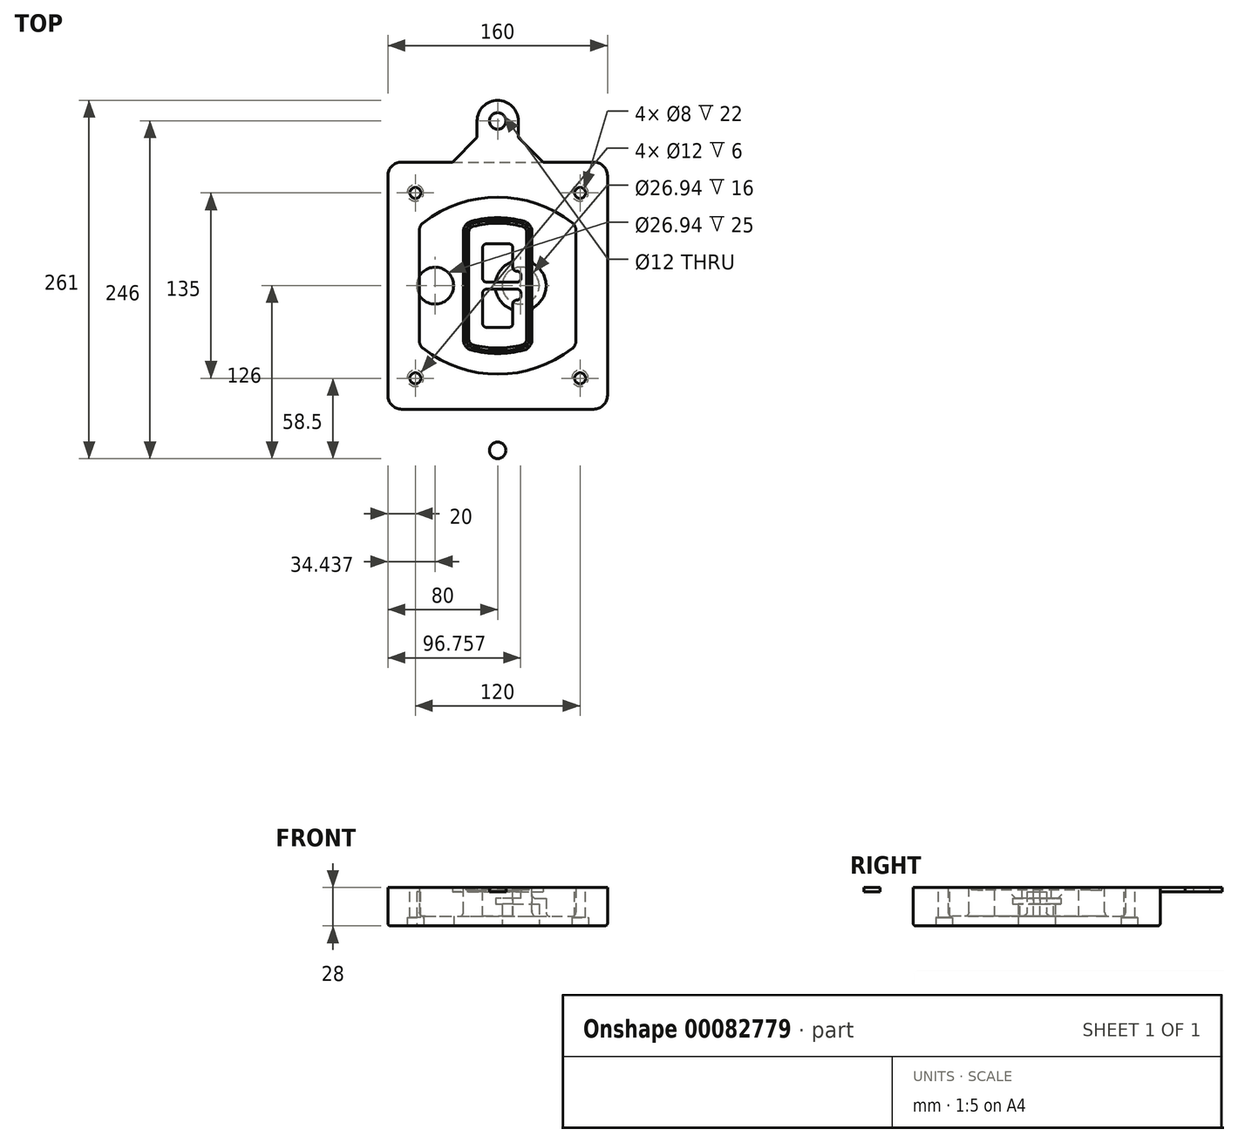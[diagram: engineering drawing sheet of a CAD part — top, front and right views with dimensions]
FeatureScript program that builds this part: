
annotation { "Feature Type Name" : "Feature", "Feature Type Description" : "" }
export const myFeature = defineFeature(function(context is Context, id is Id, definition is map)
    precondition{}
    {
        {
            var Q0;
            Q0=qCreatedBy(makeId("Top.planeOp"),FACE);
            var sketch = newSketch(context, id + "F0", { "sketchPlane" : qUnion([Q0])});
            skPoint(sketch, "E0.rect.middle", {"position": v(0, 0) * mm});
            skLineSegment(sketch, "E1.bottom", {"start": v(-70, -90) * mm, "end": v(70, -90) * mm});
            skLineSegment(sketch, "E1.top", {"start": v(-70, 90) * mm, "end": v(70, 90) * mm});
            skLineSegment(sketch, "E1.left", {"start": v(-80, -80) * mm, "end": v(-80, 80) * mm});
            skLineSegment(sketch, "E1.right", {"start": v(80, -80) * mm, "end": v(80, 80) * mm});
            skLineSegment(sketch, "E2", {"start": v(-80, 90) * mm, "end": v(80, -90) * mm, "construction": true});
            skLineSegment(sketch, "E3", {"start": v(80, 90) * mm, "end": v(-80, -90) * mm, "construction": true});
            skCircle(sketch, "E4", {"center": v(-60, 67.5) * mm, "radius": 4 * mm});
            skCircle(sketch, "E5", {"center": v(60, 67.5) * mm, "radius": 4 * mm});
            skCircle(sketch, "E6", {"center": v(60, -67.5) * mm, "radius": 4 * mm});
            skCircle(sketch, "E7", {"center": v(-60, -67.5) * mm, "radius": 4 * mm});
            skLineSegment(sketch, "E8", {"start": v(-60, 67.5) * mm, "end": v(60, 67.5) * mm, "construction": true});
            skLineSegment(sketch, "E9", {"start": v(60, 67.5) * mm, "end": v(60, -67.5) * mm, "construction": true});
            skLineSegment(sketch, "E10", {"start": v(60, -67.5) * mm, "end": v(-60, -67.5) * mm, "construction": true});
            skLineSegment(sketch, "E11", {"start": v(-60, -67.5) * mm, "end": v(-60, 67.5) * mm, "construction": true});
            skLineSegment(sketch, "E12", {"start": v(-60, 40.3) * mm, "end": v(-60, -40.3) * mm});
            skLineSegment(sketch, "E13", {"start": v(60, 40.3) * mm, "end": v(60, -40.3) * mm});
            skArc(sketch, "E14", {"start": v(56.15, 48.18) * mm, "mid": v(0, 67.5) * mm, "end": v(-56.15, 48.18) * mm});
            skArc(sketch, "E15", {"start": v(-56.15, -48.18) * mm, "mid": v(0, -67.5) * mm, "end": v(56.15, -48.18) * mm});
            skLineSegment(sketch, "E16", {"start": v(-60, 0) * mm, "end": v(60, 0) * mm, "construction": true});
            skPoint(sketch, "E17.visualSharp", {"position": v(-60, -45) * mm});
            skArc(sketch, "E17.filletArc", {"start": v(-60, -40.3) * mm, "mid": v(-58.99, -44.68) * mm, "end": v(-56.15, -48.18) * mm});
            skPoint(sketch, "E18.visualSharp", {"position": v(-60, 45) * mm});
            skArc(sketch, "E18.filletArc", {"start": v(-56.15, 48.18) * mm, "mid": v(-58.99, 44.68) * mm, "end": v(-60, 40.3) * mm});
            skPoint(sketch, "E19.visualSharp", {"position": v(60, 45) * mm});
            skArc(sketch, "E19.filletArc", {"start": v(60, 40.3) * mm, "mid": v(58.99, 44.68) * mm, "end": v(56.15, 48.18) * mm});
            skPoint(sketch, "E20.visualSharp", {"position": v(60, -45) * mm});
            skArc(sketch, "E20.filletArc", {"start": v(56.15, -48.18) * mm, "mid": v(58.99, -44.68) * mm, "end": v(60, -40.3) * mm});
            skPoint(sketch, "E21.visualSharp", {"position": v(-80, 90) * mm});
            skArc(sketch, "E21.filletArc", {"start": v(-70, 90) * mm, "mid": v(-77.07, 87.07) * mm, "end": v(-80, 80) * mm});
            skPoint(sketch, "E22.visualSharp", {"position": v(80, 90) * mm});
            skArc(sketch, "E22.filletArc", {"start": v(80, 80) * mm, "mid": v(77.07, 87.07) * mm, "end": v(70, 90) * mm});
            skPoint(sketch, "E23.visualSharp", {"position": v(80, -90) * mm});
            skArc(sketch, "E23.filletArc", {"start": v(70, -90) * mm, "mid": v(77.07, -87.07) * mm, "end": v(80, -80) * mm});
            skPoint(sketch, "E24.visualSharp", {"position": v(-80, -90) * mm});
            skArc(sketch, "E24.filletArc", {"start": v(-80, -80) * mm, "mid": v(-77.07, -87.07) * mm, "end": v(-70, -90) * mm});
            skArc(sketch, "E25.0", {"start": v(57, 40.3) * mm, "mid": v(56.3, 43.36) * mm, "end": v(54.3, 45.81) * mm});
            skLineSegment(sketch, "E25.1", {"start": v(57, 40.3) * mm, "end": v(57, -40.3) * mm});
            skArc(sketch, "E25.2", {"start": v(54.3, -45.81) * mm, "mid": v(56.3, -43.36) * mm, "end": v(57, -40.3) * mm});
            skArc(sketch, "E25.3", {"start": v(-54.3, -45.81) * mm, "mid": v(0, -64.5) * mm, "end": v(54.3, -45.81) * mm});
            skArc(sketch, "E25.4", {"start": v(-57, -40.3) * mm, "mid": v(-56.3, -43.36) * mm, "end": v(-54.3, -45.81) * mm});
            skArc(sketch, "E25.5", {"start": v(54.3, 45.81) * mm, "mid": v(0, 64.5) * mm, "end": v(-54.3, 45.81) * mm});
            skLineSegment(sketch, "E25.6", {"start": v(-57, 40.3) * mm, "end": v(-57, -40.3) * mm});
            skArc(sketch, "E25.7", {"start": v(-54.3, 45.81) * mm, "mid": v(-56.3, 43.36) * mm, "end": v(-57, 40.3) * mm});
            skArc(sketch, "E26.0", {"start": v(-58.62, 51.33) * mm, "mid": v(-62.58, 46.43) * mm, "end": v(-64, 40.3) * mm});
            skArc(sketch, "E26.1", {"start": v(58.62, 51.33) * mm, "mid": v(0, 71.5) * mm, "end": v(-58.62, 51.33) * mm});
            skArc(sketch, "E26.2", {"start": v(64, 40.3) * mm, "mid": v(62.58, 46.43) * mm, "end": v(58.62, 51.33) * mm});
            skLineSegment(sketch, "E26.3", {"start": v(64, 40.3) * mm, "end": v(64, -40.3) * mm});
            skArc(sketch, "E26.4", {"start": v(58.62, -51.33) * mm, "mid": v(62.58, -46.43) * mm, "end": v(64, -40.3) * mm});
            skLineSegment(sketch, "E26.5", {"start": v(-64, 40.3) * mm, "end": v(-64, -40.3) * mm});
            skArc(sketch, "E26.6", {"start": v(-58.62, -51.33) * mm, "mid": v(0, -71.5) * mm, "end": v(58.62, -51.33) * mm});
            skArc(sketch, "E26.7", {"start": v(-64, -40.3) * mm, "mid": v(-62.58, -46.43) * mm, "end": v(-58.62, -51.33) * mm});
            skSolve(sketch);
        }
        {
            var Q0;
            Q0=makeQuery(id+"F0.imprint","IMPRINT",FACE,{"disambiguationData":[TD([[makeQuery(id+"F0.imprint","IMPRINT",EDGE,{"derivedFrom":sQuery(id+"F0.wireOp",EDGE,"E1.bottom")}),1.0]])]});
            var Q1;
            Q1=makeQuery(id+"F0.imprint","IMPRINT",FACE,{"disambiguationData":[TD([[makeQuery(id+"F0.imprint","IMPRINT",EDGE,{"derivedFrom":sQuery(id+"F0.wireOp",EDGE,"E12")}),1.0]])]});
            var Q2;
            Q2=makeQuery(id+"F0.imprint","IMPRINT",FACE,{"disambiguationData":[TD([[makeQuery(id+"F0.imprint","IMPRINT",EDGE,{"derivedFrom":sQuery(id+"F0.wireOp",EDGE,"E25.0")}),1.0]])]});
            var Q3;
            Q3=makeQuery(id+"F0.imprint","IMPRINT",FACE,{"disambiguationData":[TD([[makeQuery(id+"F0.imprint","IMPRINT",EDGE,{"derivedFrom":sQuery(id+"F0.wireOp",EDGE,"E12")}),-1.0]])]});
            extrude(context, id + "F1", {"entities" : qUnion([Q0, Q1, Q2, Q3]), "oppositeDirection" : true, "depth" : 25 * mm});
        }
        {
            var Q0;
            Q0=makeQuery(id+"F0.imprint","IMPRINT",FACE,{"disambiguationData":[TD([[makeQuery(id+"F0.imprint","IMPRINT",EDGE,{"derivedFrom":sQuery(id+"F0.wireOp",EDGE,"E12")}),1.0]])]});
            extrude(context, id + "F2", {"entities" : qUnion([Q0]), "operationType" : NewBodyOperationType.ADD, "depth" : 3 * mm});
        }
        {
            var Q0;
            Q0=makeQuery(id+"F0.imprint","IMPRINT",FACE,{"disambiguationData":[TD([[makeQuery(id+"F0.imprint","IMPRINT",EDGE,{"derivedFrom":sQuery(id+"F0.wireOp",EDGE,"E25.0")}),1.0]])]});
            extrude(context, id + "F3", {"entities" : qUnion([Q0]), "operationType" : NewBodyOperationType.REMOVE, "oppositeDirection" : true, "depth" : 18 * mm});
        }
        {
            var Q0;
            Q0=makeQuery(id+"F2.opExtrude","CAP_FACE",FACE,{"disambiguationData":[OSD([sQuery(id+"F0.wireOp",EDGE,"E12"),sQuery(id+"F0.wireOp",EDGE,"E13"),sQuery(id+"F0.wireOp",EDGE,"E14"),sQuery(id+"F0.wireOp",EDGE,"E15"),sQuery(id+"F0.wireOp",EDGE,"E17.filletArc"),sQuery(id+"F0.wireOp",EDGE,"E18.filletArc"),sQuery(id+"F0.wireOp",EDGE,"E19.filletArc"),sQuery(id+"F0.wireOp",EDGE,"E20.filletArc"),sQuery(id+"F0.wireOp",EDGE,"E25.0"),sQuery(id+"F0.wireOp",EDGE,"E25.1"),sQuery(id+"F0.wireOp",EDGE,"E25.2"),sQuery(id+"F0.wireOp",EDGE,"E25.3"),sQuery(id+"F0.wireOp",EDGE,"E25.4"),sQuery(id+"F0.wireOp",EDGE,"E25.5"),sQuery(id+"F0.wireOp",EDGE,"E25.6"),sQuery(id+"F0.wireOp",EDGE,"E25.7")])],"isStart":false});
            var sketch = newSketch(context, id + "F4", { "sketchPlane" : qUnion([Q0])});
            skArc(sketch, "E27.0", {"start": v(-19.08, -46.97) * mm, "mid": v(0, -49.5) * mm, "end": v(19.08, -46.97) * mm});
            skArc(sketch, "E28.0", {"start": v(19.08, 46.97) * mm, "mid": v(0, 49.5) * mm, "end": v(-19.08, 46.97) * mm});
            skLineSegment(sketch, "E29", {"start": v(-25, 39.25) * mm, "end": v(-25, -39.25) * mm});
            skLineSegment(sketch, "E30", {"start": v(25, 39.25) * mm, "end": v(25, -39.25) * mm});
            skLineSegment(sketch, "E31", {"start": v(-25, 45.1) * mm, "end": v(25, 45.1) * mm, "construction": true});
            skLineSegment(sketch, "E32", {"start": v(-25, -45.1) * mm, "end": v(25, -45.1) * mm, "construction": true});
            skPoint(sketch, "E33.visualSharp", {"position": v(-25, 45.1) * mm});
            skArc(sketch, "E33.filletArc", {"start": v(-19.08, 46.97) * mm, "mid": v(-23.35, 44.11) * mm, "end": v(-25, 39.25) * mm});
            skPoint(sketch, "E34.visualSharp", {"position": v(25, 45.1) * mm});
            skArc(sketch, "E34.filletArc", {"start": v(25, 39.25) * mm, "mid": v(23.35, 44.11) * mm, "end": v(19.08, 46.97) * mm});
            skPoint(sketch, "E35.visualSharp", {"position": v(25, -45.1) * mm});
            skArc(sketch, "E35.filletArc", {"start": v(19.08, -46.97) * mm, "mid": v(23.35, -44.11) * mm, "end": v(25, -39.25) * mm});
            skPoint(sketch, "E36.visualSharp", {"position": v(-25, -45.1) * mm});
            skArc(sketch, "E36.filletArc", {"start": v(-25, -39.25) * mm, "mid": v(-23.35, -44.11) * mm, "end": v(-19.08, -46.97) * mm});
            skArc(sketch, "E37.0", {"start": v(54.3, 45.81) * mm, "mid": v(0, 64.5) * mm, "end": v(-54.3, 45.81) * mm});
            skArc(sketch, "E37.1", {"start": v(-54.3, 45.81) * mm, "mid": v(-56.3, 43.36) * mm, "end": v(-57, 40.3) * mm});
            skLineSegment(sketch, "E37.2", {"start": v(-57, 40.3) * mm, "end": v(-57, -40.3) * mm});
            skArc(sketch, "E37.3", {"start": v(-57, -40.3) * mm, "mid": v(-56.3, -43.36) * mm, "end": v(-54.3, -45.81) * mm});
            skArc(sketch, "E37.4", {"start": v(-54.3, -45.81) * mm, "mid": v(0, -64.5) * mm, "end": v(54.3, -45.81) * mm});
            skArc(sketch, "E37.5", {"start": v(54.3, -45.81) * mm, "mid": v(56.3, -43.36) * mm, "end": v(57, -40.3) * mm});
            skLineSegment(sketch, "E37.6", {"start": v(57, 40.3) * mm, "end": v(57, -40.3) * mm});
            skArc(sketch, "E37.7", {"start": v(57, 40.3) * mm, "mid": v(56.3, 43.36) * mm, "end": v(54.3, 45.81) * mm});
            skLineSegment(sketch, "E38.0", {"start": v(23, 39.25) * mm, "end": v(23, -39.25) * mm});
            skArc(sketch, "E38.1", {"start": v(18.56, -45.04) * mm, "mid": v(21.76, -42.9) * mm, "end": v(23, -39.25) * mm});
            skArc(sketch, "E38.2", {"start": v(-18.56, -45.04) * mm, "mid": v(0, -47.5) * mm, "end": v(18.56, -45.04) * mm});
            skArc(sketch, "E38.3", {"start": v(-23, -39.25) * mm, "mid": v(-21.76, -42.9) * mm, "end": v(-18.56, -45.04) * mm});
            skLineSegment(sketch, "E38.4", {"start": v(-23, 39.25) * mm, "end": v(-23, -39.25) * mm});
            skArc(sketch, "E38.5", {"start": v(23, 39.25) * mm, "mid": v(21.76, 42.9) * mm, "end": v(18.56, 45.04) * mm});
            skArc(sketch, "E38.6", {"start": v(-18.56, 45.04) * mm, "mid": v(-21.76, 42.9) * mm, "end": v(-23, 39.25) * mm});
            skArc(sketch, "E38.7", {"start": v(18.56, 45.04) * mm, "mid": v(0, 47.5) * mm, "end": v(-18.56, 45.04) * mm});
            skArc(sketch, "E39.0", {"start": v(21, 39.25) * mm, "mid": v(20.18, 41.68) * mm, "end": v(18.04, 43.1) * mm});
            skLineSegment(sketch, "E39.1", {"start": v(21, 39.25) * mm, "end": v(21, -39.25) * mm});
            skArc(sketch, "E39.2", {"start": v(18.04, -43.1) * mm, "mid": v(20.18, -41.68) * mm, "end": v(21, -39.25) * mm});
            skArc(sketch, "E39.3", {"start": v(-18.04, -43.1) * mm, "mid": v(0, -45.5) * mm, "end": v(18.04, -43.1) * mm});
            skArc(sketch, "E39.4", {"start": v(-21, -39.25) * mm, "mid": v(-20.18, -41.68) * mm, "end": v(-18.04, -43.1) * mm});
            skArc(sketch, "E39.5", {"start": v(18.04, 43.1) * mm, "mid": v(0, 45.5) * mm, "end": v(-18.04, 43.1) * mm});
            skLineSegment(sketch, "E39.6", {"start": v(-21, 39.25) * mm, "end": v(-21, -39.25) * mm});
            skArc(sketch, "E39.7", {"start": v(-18.04, 43.1) * mm, "mid": v(-20.18, 41.68) * mm, "end": v(-21, 39.25) * mm});
            skLineSegment(sketch, "E40", {"start": v(-25, 0) * mm, "end": v(25, 0) * mm, "construction": true});
            skLineSegment(sketch, "E41", {"start": v(-11, 5.5) * mm, "end": v(-11, 27.5) * mm});
            skLineSegment(sketch, "E42", {"start": v(-8, 30.5) * mm, "end": v(8, 30.5) * mm});
            skLineSegment(sketch, "E43", {"start": v(11, 27.5) * mm, "end": v(11, 13.5) * mm});
            skLineSegment(sketch, "E44", {"start": v(14, 10.5) * mm, "end": v(14, 10.5) * mm});
            skLineSegment(sketch, "E45", {"start": v(17, 7.5) * mm, "end": v(17, 5.5) * mm});
            skLineSegment(sketch, "E46", {"start": v(14, 2.5) * mm, "end": v(-8, 2.5) * mm});
            skPoint(sketch, "E47.visualSharp", {"position": v(-11, 30.5) * mm});
            skArc(sketch, "E47.filletArc", {"start": v(-8, 30.5) * mm, "mid": v(-10.12, 29.62) * mm, "end": v(-11, 27.5) * mm});
            skPoint(sketch, "E48.visualSharp", {"position": v(11, 30.5) * mm});
            skArc(sketch, "E48.filletArc", {"start": v(11, 27.5) * mm, "mid": v(10.12, 29.62) * mm, "end": v(8, 30.5) * mm});
            skPoint(sketch, "E49.visualSharp", {"position": v(11, 10.5) * mm});
            skArc(sketch, "E49.filletArc", {"start": v(11, 13.5) * mm, "mid": v(11.88, 11.38) * mm, "end": v(14, 10.5) * mm});
            skPoint(sketch, "E50.visualSharp", {"position": v(17, 10.5) * mm});
            skArc(sketch, "E50.filletArc", {"start": v(17, 7.5) * mm, "mid": v(16.12, 9.62) * mm, "end": v(14, 10.5) * mm});
            skPoint(sketch, "E51.visualSharp", {"position": v(17, 2.5) * mm});
            skArc(sketch, "E51.filletArc", {"start": v(14, 2.5) * mm, "mid": v(16.12, 3.38) * mm, "end": v(17, 5.5) * mm});
            skPoint(sketch, "E52.visualSharp", {"position": v(-11, 2.5) * mm});
            skArc(sketch, "E52.filletArc", {"start": v(-11, 5.5) * mm, "mid": v(-10.12, 3.38) * mm, "end": v(-8, 2.5) * mm});
            skLineSegment(sketch, "E53.0.MirrorCS", {"start": v(14, -2.5) * mm, "end": v(-8, -2.5) * mm});
            skArc(sketch, "E54.0.MirrorCS", {"start": v(-11, -5.5) * mm, "mid": v(-10.12, -3.38) * mm, "end": v(-8, -2.5) * mm});
            skLineSegment(sketch, "E55.0.MirrorCS", {"start": v(-11, -5.5) * mm, "end": v(-11, -27.5) * mm});
            skArc(sketch, "E56.0.MirrorCS", {"start": v(-8, -30.5) * mm, "mid": v(-10.12, -29.62) * mm, "end": v(-11, -27.5) * mm});
            skLineSegment(sketch, "E57.0.MirrorCS", {"start": v(-8, -30.5) * mm, "end": v(8, -30.5) * mm});
            skArc(sketch, "E58.0.MirrorCS", {"start": v(11, -27.5) * mm, "mid": v(10.12, -29.62) * mm, "end": v(8, -30.5) * mm});
            skLineSegment(sketch, "E59.0.MirrorCS", {"start": v(11, -27.5) * mm, "end": v(11, -13.5) * mm});
            skArc(sketch, "E60.0.MirrorCS", {"start": v(11, -13.5) * mm, "mid": v(11.88, -11.38) * mm, "end": v(14, -10.5) * mm});
            skArc(sketch, "E61.0.MirrorCS", {"start": v(17, -7.5) * mm, "mid": v(16.12, -9.62) * mm, "end": v(14, -10.5) * mm});
            skLineSegment(sketch, "E62.0.MirrorCS", {"start": v(17, -7.5) * mm, "end": v(17, -5.5) * mm});
            skArc(sketch, "E63.0.MirrorCS", {"start": v(14, -2.5) * mm, "mid": v(16.12, -3.38) * mm, "end": v(17, -5.5) * mm});
            skSolve(sketch);
        }
        {
            var Q0;
            Q0=makeQuery(id+"F4.imprint","IMPRINT",FACE,{"disambiguationData":[TD([[makeQuery(id+"F4.imprint","IMPRINT",EDGE,{"derivedFrom":sQuery(id+"F4.wireOp",EDGE,"E27.0")}),1.0]])]});
            var Q1;
            Q1=makeQuery(id+"F4.imprint","IMPRINT",FACE,{"disambiguationData":[TD([[makeQuery(id+"F4.imprint","IMPRINT",EDGE,{"derivedFrom":sQuery(id+"F4.wireOp",EDGE,"E38.0")}),-1.0]])]});
            var Q2;
            Q2=makeQuery(id+"F4.imprint","IMPRINT",FACE,{"disambiguationData":[TD([[makeQuery(id+"F4.imprint","IMPRINT",EDGE,{"derivedFrom":sQuery(id+"F4.wireOp",EDGE,"E39.0")}),1.0]])]});
            extrude(context, id + "F5", {"entities" : qUnion([Q0, Q1, Q2]), "operationType" : NewBodyOperationType.ADD, "endBound" : BoundingType.UP_TO_NEXT, "oppositeDirection" : true, "depth" : 25 * mm});
        }
        {
            var Q0;
            Q0=makeQuery(id+"F4.imprint","IMPRINT",FACE,{"disambiguationData":[TD([[makeQuery(id+"F4.imprint","IMPRINT",EDGE,{"derivedFrom":sQuery(id+"F4.wireOp",EDGE,"E38.0")}),-1.0]])]});
            extrude(context, id + "F6", {"entities" : qUnion([Q0]), "operationType" : NewBodyOperationType.REMOVE, "oppositeDirection" : true, "depth" : 2 * mm});
        }
        {
            var Q0;
            Q0=makeQuery(id+"F1.opExtrude","CAP_FACE",FACE,{"disambiguationData":[OSD([sQuery(id+"F0.wireOp",EDGE,"E1.bottom"),sQuery(id+"F0.wireOp",EDGE,"E1.top"),sQuery(id+"F0.wireOp",EDGE,"E1.left"),sQuery(id+"F0.wireOp",EDGE,"E1.right"),sQuery(id+"F0.wireOp",EDGE,"E4"),sQuery(id+"F0.wireOp",EDGE,"E5"),sQuery(id+"F0.wireOp",EDGE,"E6"),sQuery(id+"F0.wireOp",EDGE,"E7"),sQuery(id+"F0.wireOp",EDGE,"E21.filletArc"),sQuery(id+"F0.wireOp",EDGE,"E22.filletArc"),sQuery(id+"F0.wireOp",EDGE,"E23.filletArc"),sQuery(id+"F0.wireOp",EDGE,"E24.filletArc")])],"isStart":false});
            var sketch = newSketch(context, id + "F7", { "sketchPlane" : qUnion([Q0])});
            skCircle(sketch, "E64", {"center": v(16.76, 0) * mm, "radius": 13.47 * mm});
            skCircle(sketch, "E65", {"center": v(-45.56, 0) * mm, "radius": 13.47 * mm});
            skLineSegment(sketch, "E66", {"start": v(80, 0) * mm, "end": v(-80, 0) * mm});
            skCircle(sketch, "E67", {"center": v(16.76, 0) * mm, "radius": 18.47 * mm});
            skCircle(sketch, "E68", {"center": v(60, -67.5) * mm, "radius": 6 * mm});
            skCircle(sketch, "E69", {"center": v(-60, -67.5) * mm, "radius": 6 * mm});
            skCircle(sketch, "E70", {"center": v(-60, 67.5) * mm, "radius": 6 * mm});
            skCircle(sketch, "E71", {"center": v(60, 67.5) * mm, "radius": 6 * mm});
            skSolve(sketch);
        }
        {
            var Q0;
            {var subQ1=sQuery(id+"F7.wireOp",EDGE,"E66");var subQ4=sQuery(id+"F7.wireOp",EDGE,"E64");var subQ6=makeQuery(id+"F7.imprint","INTERSECT",VERTEX,{"disambiguationData":[OD(0.0)],"derivedFrom":[subQ4,subQ1]});Q0=makeQuery(id+"F7.imprint","IMPRINT",FACE,{"disambiguationData":[TD([[makeQuery(id+"F7.imprint","IMPRINT",EDGE,{"disambiguationData":[TD([[subQ6,-1.0]])],"derivedFrom":subQ4}),-1.0]])]});}
            var Q1;
            {var subQ0=sQuery(id+"F7.wireOp",EDGE,"E66");var subQ1=sQuery(id+"F7.wireOp",EDGE,"E64");var subQ3=makeQuery(id+"F7.imprint","INTERSECT",VERTEX,{"disambiguationData":[OD(0.0)],"derivedFrom":[subQ1,subQ0]});Q1=makeQuery(id+"F7.imprint","IMPRINT",FACE,{"disambiguationData":[TD([[makeQuery(id+"F7.imprint","IMPRINT",EDGE,{"disambiguationData":[TD([[subQ3,-1.0]])],"derivedFrom":subQ1}),1.0]])]});}
            var Q2;
            {var subQ0=sQuery(id+"F7.wireOp",EDGE,"E66");var subQ1=sQuery(id+"F7.wireOp",EDGE,"E64");var subQ3=makeQuery(id+"F7.imprint","INTERSECT",VERTEX,{"disambiguationData":[OD(0.0)],"derivedFrom":[subQ1,subQ0]});Q2=makeQuery(id+"F7.imprint","IMPRINT",FACE,{"disambiguationData":[TD([[makeQuery(id+"F7.imprint","IMPRINT",EDGE,{"disambiguationData":[TD([[subQ3,1.0]])],"derivedFrom":subQ1}),1.0]])]});}
            var Q3;
            {var subQ1=sQuery(id+"F7.wireOp",EDGE,"E66");var subQ4=sQuery(id+"F7.wireOp",EDGE,"E64");var subQ6=makeQuery(id+"F7.imprint","INTERSECT",VERTEX,{"disambiguationData":[OD(0.0)],"derivedFrom":[subQ4,subQ1]});Q3=makeQuery(id+"F7.imprint","IMPRINT",FACE,{"disambiguationData":[TD([[makeQuery(id+"F7.imprint","IMPRINT",EDGE,{"disambiguationData":[TD([[subQ6,1.0]])],"derivedFrom":subQ4}),-1.0]])]});}
            extrude(context, id + "F8", {"entities" : qUnion([Q0, Q1, Q2, Q3]), "operationType" : NewBodyOperationType.ADD, "oppositeDirection" : true, "depth" : 20 * mm});
        }
        {
            var Q0;
            {var subQ0=sQuery(id+"F7.wireOp",EDGE,"E66");var subQ1=sQuery(id+"F7.wireOp",EDGE,"E64");var subQ3=makeQuery(id+"F7.imprint","INTERSECT",VERTEX,{"disambiguationData":[OD(0.0)],"derivedFrom":[subQ1,subQ0]});Q0=makeQuery(id+"F7.imprint","IMPRINT",FACE,{"disambiguationData":[TD([[makeQuery(id+"F7.imprint","IMPRINT",EDGE,{"disambiguationData":[TD([[subQ3,-1.0]])],"derivedFrom":subQ1}),1.0]])]});}
            var Q1;
            {var subQ0=sQuery(id+"F7.wireOp",EDGE,"E66");var subQ1=sQuery(id+"F7.wireOp",EDGE,"E64");var subQ3=makeQuery(id+"F7.imprint","INTERSECT",VERTEX,{"disambiguationData":[OD(0.0)],"derivedFrom":[subQ1,subQ0]});Q1=makeQuery(id+"F7.imprint","IMPRINT",FACE,{"disambiguationData":[TD([[makeQuery(id+"F7.imprint","IMPRINT",EDGE,{"disambiguationData":[TD([[subQ3,1.0]])],"derivedFrom":subQ1}),1.0]])]});}
            extrude(context, id + "F9", {"entities" : qUnion([Q0, Q1]), "operationType" : NewBodyOperationType.REMOVE, "oppositeDirection" : true, "depth" : 16 * mm});
        }
        {
            var Q0;
            {var subQ0=sQuery(id+"F7.wireOp",EDGE,"E66");var subQ1=sQuery(id+"F7.wireOp",EDGE,"E65");var subQ3=makeQuery(id+"F7.imprint","INTERSECT",VERTEX,{"disambiguationData":[OD(0.0)],"derivedFrom":[subQ1,subQ0]});Q0=makeQuery(id+"F7.imprint","IMPRINT",FACE,{"disambiguationData":[TD([[makeQuery(id+"F7.imprint","IMPRINT",EDGE,{"disambiguationData":[TD([[subQ3,-1.0]])],"derivedFrom":subQ1}),1.0]])]});}
            var Q1;
            {var subQ0=sQuery(id+"F7.wireOp",EDGE,"E66");var subQ1=sQuery(id+"F7.wireOp",EDGE,"E65");var subQ3=makeQuery(id+"F7.imprint","INTERSECT",VERTEX,{"disambiguationData":[OD(0.0)],"derivedFrom":[subQ1,subQ0]});Q1=makeQuery(id+"F7.imprint","IMPRINT",FACE,{"disambiguationData":[TD([[makeQuery(id+"F7.imprint","IMPRINT",EDGE,{"disambiguationData":[TD([[subQ3,1.0]])],"derivedFrom":subQ1}),1.0]])]});}
            extrude(context, id + "F10", {"entities" : qUnion([Q0, Q1]), "operationType" : NewBodyOperationType.REMOVE, "oppositeDirection" : true, "depth" : 25 * mm});
        }
        {
            var Q0;
            Q0=makeQuery(id+"F7.imprint","IMPRINT",FACE,{"disambiguationData":[TD([[makeQuery(id+"F7.imprint","IMPRINT",EDGE,{"derivedFrom":sQuery(id+"F7.wireOp",EDGE,"E68")}),1.0]])]});
            var Q1;
            Q1=makeQuery(id+"F7.imprint","IMPRINT",FACE,{"disambiguationData":[TD([[makeQuery(id+"F7.imprint","IMPRINT",EDGE,{"derivedFrom":makeQuery(id+"F1.opExtrude","CAP_EDGE",EDGE,{"disambiguationData":[OSD([sQuery(id+"F0.wireOp",EDGE,"E5")])],"isStart":false})}),-1.0]])]});
            var Q2;
            Q2=makeQuery(id+"F7.imprint","IMPRINT",FACE,{"disambiguationData":[TD([[makeQuery(id+"F7.imprint","IMPRINT",EDGE,{"derivedFrom":sQuery(id+"F7.wireOp",EDGE,"E69")}),1.0]])]});
            var Q3;
            Q3=makeQuery(id+"F7.imprint","IMPRINT",FACE,{"disambiguationData":[TD([[makeQuery(id+"F7.imprint","IMPRINT",EDGE,{"derivedFrom":makeQuery(id+"F1.opExtrude","CAP_EDGE",EDGE,{"disambiguationData":[OSD([sQuery(id+"F0.wireOp",EDGE,"E4")])],"isStart":false})}),-1.0]])]});
            var Q4;
            Q4=makeQuery(id+"F7.imprint","IMPRINT",FACE,{"disambiguationData":[TD([[makeQuery(id+"F7.imprint","IMPRINT",EDGE,{"derivedFrom":sQuery(id+"F7.wireOp",EDGE,"E70")}),1.0]])]});
            var Q5;
            Q5=makeQuery(id+"F7.imprint","IMPRINT",FACE,{"disambiguationData":[TD([[makeQuery(id+"F7.imprint","IMPRINT",EDGE,{"derivedFrom":makeQuery(id+"F1.opExtrude","CAP_EDGE",EDGE,{"disambiguationData":[OSD([sQuery(id+"F0.wireOp",EDGE,"E7")])],"isStart":false})}),-1.0]])]});
            var Q6;
            Q6=makeQuery(id+"F7.imprint","IMPRINT",FACE,{"disambiguationData":[TD([[makeQuery(id+"F7.imprint","IMPRINT",EDGE,{"derivedFrom":sQuery(id+"F7.wireOp",EDGE,"E71")}),1.0]])]});
            var Q7;
            Q7=makeQuery(id+"F7.imprint","IMPRINT",FACE,{"disambiguationData":[TD([[makeQuery(id+"F7.imprint","IMPRINT",EDGE,{"derivedFrom":makeQuery(id+"F1.opExtrude","CAP_EDGE",EDGE,{"disambiguationData":[OSD([sQuery(id+"F0.wireOp",EDGE,"E6")])],"isStart":false})}),-1.0]])]});
            extrude(context, id + "F11", {"entities" : qUnion([Q0, Q1, Q2, Q3, Q4, Q5, Q6, Q7]), "operationType" : NewBodyOperationType.REMOVE, "oppositeDirection" : true, "depth" : 6 * mm});
        }
        {
            var Q0;
            Q0=makeQuery(id+"F9.boolean.opBoolean","COPY",FACE,{"derivedFrom":makeQuery(id+"F9.opExtrude","CAP_FACE",FACE,{"disambiguationData":[OSD([sQuery(id+"F7.wireOp",EDGE,"E64")])],"isStart":false})});
            var sketch = newSketch(context, id + "F12", { "sketchPlane" : qUnion([Q0])});
            skArc(sketch, "E72.0", {"start": v(11, 17.55) * mm, "mid": v(2.57, 11.82) * mm, "end": v(-1.54, 2.5) * mm});
            skArc(sketch, "E72.1", {"start": v(-1.54, -2.5) * mm, "mid": v(2.57, -11.82) * mm, "end": v(11, -17.55) * mm});
            skLineSegment(sketch, "E73", {"start": v(-1.54, -2.5) * mm, "end": v(14, -2.5) * mm});
            skLineSegment(sketch, "E74.0", {"start": v(14, 2.5) * mm, "end": v(-1.54, 2.5) * mm});
            skArc(sketch, "E74.1", {"start": v(14, 2.5) * mm, "mid": v(16.12, 3.38) * mm, "end": v(17, 5.5) * mm});
            skLineSegment(sketch, "E74.2", {"start": v(17, 7.5) * mm, "end": v(17, 5.5) * mm});
            skArc(sketch, "E74.3", {"start": v(17, 7.5) * mm, "mid": v(16.12, 9.62) * mm, "end": v(14, 10.5) * mm});
            skArc(sketch, "E74.4", {"start": v(11, 13.5) * mm, "mid": v(11.88, 11.38) * mm, "end": v(14, 10.5) * mm});
            skLineSegment(sketch, "E74.5", {"start": v(11, 17.55) * mm, "end": v(11, 13.5) * mm});
            skLineSegment(sketch, "E74.7", {"start": v(14, -2.5) * mm, "end": v(-1.54, -2.5) * mm});
            skArc(sketch, "E74.8", {"start": v(14, -2.5) * mm, "mid": v(16.12, -3.38) * mm, "end": v(17, -5.5) * mm});
            skLineSegment(sketch, "E74.9", {"start": v(17, -7.5) * mm, "end": v(17, -5.5) * mm});
            skArc(sketch, "E74.10", {"start": v(17, -7.5) * mm, "mid": v(16.12, -9.62) * mm, "end": v(14, -10.5) * mm});
            skArc(sketch, "E74.11", {"start": v(11, -13.5) * mm, "mid": v(11.88, -11.38) * mm, "end": v(14, -10.5) * mm});
            skLineSegment(sketch, "E74.12", {"start": v(11, -17.55) * mm, "end": v(11, -13.5) * mm});
            skPoint(sketch, "E75.orphan", {"position": v(11, -27.5) * mm});
            skPoint(sketch, "E76.orphan", {"position": v(-8, -2.5) * mm});
            skPoint(sketch, "E77.orphan", {"position": v(-8, 2.5) * mm});
            skPoint(sketch, "E78.orphan", {"position": v(11, 27.5) * mm});
            skSolve(sketch);
        }
        {
            var Q0;
            {var subQ7=sQuery(id+"F12.wireOp",EDGE,"E72.0");var subQ14=sQuery(id+"F12.wireOp",EDGE,"E72.1");var subQ16=sQuery(id+"F12.wireOp",EDGE,"E74.1");var subQ18=sQuery(id+"F12.wireOp",EDGE,"E74.8");Q0=qUnion([makeQuery(id+"F12.imprint","IMPRINT",FACE,{"disambiguationData":[TD([[makeQuery(id+"F12.imprint","IMPRINT",EDGE,{"derivedFrom":subQ7}),1.0]])]}),makeQuery(id+"F12.imprint","IMPRINT",FACE,{"disambiguationData":[TD([[makeQuery(id+"F12.imprint","IMPRINT",EDGE,{"derivedFrom":subQ14}),1.0]])]}),makeQuery(id+"F12.imprint","IMPRINT",FACE,{"disambiguationData":[TD([[makeQuery(id+"F12.imprint","IMPRINT",EDGE,{"derivedFrom":subQ16}),1.0]])]}),makeQuery(id+"F12.imprint","IMPRINT",FACE,{"disambiguationData":[TD([[makeQuery(id+"F12.imprint","IMPRINT",EDGE,{"derivedFrom":subQ18}),-1.0]])]})]);}
            var Q1;
            Q1=makeQuery(id+"F5.boolean.opBoolean","SPLIT",FACE,{"disambiguationData":[TD([makeQuery(id+"F5.opExtrude","SWEPT_FACE",FACE,{"disambiguationData":[OSD([sQuery(id+"F4.wireOp",EDGE,"E41")])]})])],"derivedFrom":makeQuery(id+"F3.boolean.opBoolean","COPY",FACE,{"derivedFrom":makeQuery(id+"F3.opExtrude","CAP_FACE",FACE,{"disambiguationData":[OSD([sQuery(id+"F0.wireOp",EDGE,"E25.0"),sQuery(id+"F0.wireOp",EDGE,"E25.1"),sQuery(id+"F0.wireOp",EDGE,"E25.2"),sQuery(id+"F0.wireOp",EDGE,"E25.3"),sQuery(id+"F0.wireOp",EDGE,"E25.4"),sQuery(id+"F0.wireOp",EDGE,"E25.5"),sQuery(id+"F0.wireOp",EDGE,"E25.6"),sQuery(id+"F0.wireOp",EDGE,"E25.7")])],"isStart":false})})});
            extrude(context, id + "F13", {"entities" : qUnion([Q0]), "operationType" : NewBodyOperationType.REMOVE, "endBound" : BoundingType.UP_TO_SURFACE, "endBoundEntityFace" : qUnion([Q1]), "depth" : 25 * mm});
        }
        {
            var Q0;
            Q0=makeQuery(id+"F3.boolean.opBoolean","COPY",EDGE,{"derivedFrom":makeQuery(id+"F3.opExtrude","CAP_EDGE",EDGE,{"disambiguationData":[OSD([sQuery(id+"F0.wireOp",EDGE,"E25.6")])],"isStart":false})});
            var Q1;
            Q1=makeQuery(id+"F8.boolean.opBoolean","INTERSECT",EDGE,{"derivedFrom":[makeQuery(id+"F5.opExtrude","SWEPT_FACE",FACE,{"disambiguationData":[OSD([sQuery(id+"F4.wireOp",EDGE,"E30")])]}),makeQuery(id+"F8.opExtrude","CAP_FACE",FACE,{"disambiguationData":[OSD([sQuery(id+"F7.wireOp",EDGE,"E67")])],"isStart":false})]});
            var Q2;
            Q2=makeQuery(id+"F8.boolean.opBoolean","INTERSECT",EDGE,{"disambiguationData":[OD(1.0)],"derivedFrom":[makeQuery(id+"F5.opExtrude","SWEPT_FACE",FACE,{"disambiguationData":[OSD([sQuery(id+"F4.wireOp",EDGE,"E30")])]}),makeQuery(id+"F8.opExtrude","SWEPT_FACE",FACE,{"disambiguationData":[OSD([sQuery(id+"F7.wireOp",EDGE,"E67")])]})]});
            var Q3;
            {var subQ0=sQuery(id+"F4.wireOp",EDGE,"E30");Q3=makeQuery(id+"F8.boolean.opBoolean","SPLIT",EDGE,{"disambiguationData":[TD([makeQuery(id+"F5.opExtrude","SWEPT_FACE",FACE,{"disambiguationData":[OSD([sQuery(id+"F4.wireOp",EDGE,"E35.filletArc")])]})])],"derivedFrom":makeQuery(id+"F5.opExtrude","CAP_EDGE",EDGE,{"disambiguationData":[OSD([subQ0])],"isStart":false})});}
            var Q4;
            {var subQ0=sQuery(id+"F0.wireOp",EDGE,"E25.7");var subQ1=sQuery(id+"F0.wireOp",EDGE,"E25.1");var subQ2=sQuery(id+"F0.wireOp",EDGE,"E25.6");var subQ3=sQuery(id+"F0.wireOp",EDGE,"E25.5");var subQ4=sQuery(id+"F0.wireOp",EDGE,"E25.4");var subQ5=sQuery(id+"F0.wireOp",EDGE,"E25.0");var subQ6=sQuery(id+"F0.wireOp",EDGE,"E25.2");var subQ7=sQuery(id+"F0.wireOp",EDGE,"E25.3");Q4=makeQuery(id+"F8.boolean.opBoolean","INTERSECT",EDGE,{"derivedFrom":[makeQuery(id+"F5.boolean.opBoolean","SPLIT",FACE,{"disambiguationData":[TD([makeQuery(id+"F2.opExtrude","SWEPT_FACE",FACE,{"disambiguationData":[OSD([subQ5])]})])],"derivedFrom":makeQuery(id+"F3.boolean.opBoolean","COPY",FACE,{"derivedFrom":makeQuery(id+"F3.opExtrude","CAP_FACE",FACE,{"disambiguationData":[OSD([subQ5,subQ1,subQ6,subQ7,subQ4,subQ3,subQ2,subQ0])],"isStart":false})})}),makeQuery(id+"F8.opExtrude","SWEPT_FACE",FACE,{"disambiguationData":[OSD([sQuery(id+"F7.wireOp",EDGE,"E67")])]})]});}
            var Q5;
            Q5=makeQuery(id+"F8.boolean.opBoolean","INTERSECT",EDGE,{"disambiguationData":[OD(0.0)],"derivedFrom":[makeQuery(id+"F5.opExtrude","SWEPT_FACE",FACE,{"disambiguationData":[OSD([sQuery(id+"F4.wireOp",EDGE,"E30")])]}),makeQuery(id+"F8.opExtrude","SWEPT_FACE",FACE,{"disambiguationData":[OSD([sQuery(id+"F7.wireOp",EDGE,"E67")])]})]});
            fillet(context, id + "F14", {"entities" : qUnion([Q0, Q1, Q2, Q3, Q4, Q5]), "radius" : 3 * mm, "tangentPropagation" : true, "allowEdgeOverflow" : false});
        }
        {
            var Q0;
            Q0=makeQuery(id+"F1.opExtrude","CAP_EDGE",EDGE,{"disambiguationData":[OSD([sQuery(id+"F0.wireOp",EDGE,"E1.bottom")])],"isStart":false});
            fillet(context, id + "F15", {"entities" : qUnion([Q0]), "radius" : 2 * mm, "tangentPropagation" : true, "allowEdgeOverflow" : false});
        }
        {
            var Q0;
            {var subQ0=sQuery(id+"F0.wireOp",EDGE,"E22.filletArc");var subQ1=sQuery(id+"F0.wireOp",EDGE,"E7");var subQ2=sQuery(id+"F0.wireOp",EDGE,"E6");var subQ3=sQuery(id+"F0.wireOp",EDGE,"E5");var subQ4=sQuery(id+"F0.wireOp",EDGE,"E4");var subQ5=sQuery(id+"F0.wireOp",EDGE,"E1.bottom");var subQ6=sQuery(id+"F0.wireOp",EDGE,"E21.filletArc");var subQ7=sQuery(id+"F0.wireOp",EDGE,"E1.top");var subQ8=sQuery(id+"F0.wireOp",EDGE,"E1.left");var subQ9=sQuery(id+"F0.wireOp",EDGE,"E1.right");var subQ10=sQuery(id+"F0.wireOp",EDGE,"E23.filletArc");var subQ11=sQuery(id+"F0.wireOp",EDGE,"E24.filletArc");Q0=makeQuery(id+"F2.boolean.opBoolean","SPLIT",FACE,{"disambiguationData":[TD([makeQuery(id+"F1.opExtrude","SWEPT_FACE",FACE,{"disambiguationData":[OSD([subQ5])]})])],"derivedFrom":makeQuery(id+"F1.opExtrude","CAP_FACE",FACE,{"disambiguationData":[OSD([subQ5,subQ7,subQ8,subQ9,subQ4,subQ3,subQ2,subQ1,subQ6,subQ0,subQ10,subQ11])],"isStart":true})});}
            var sketch = newSketch(context, id + "F16", { "sketchPlane" : qUnion([Q0])});
            skPoint(sketch, "E79.centerSnap0", {"position": v(0, 90) * mm});
            skLineSegment(sketch, "E80", {"start": v(0, 90) * mm, "end": v(0, 120) * mm, "construction": true});
            skCircle(sketch, "E81", {"center": v(0, 120) * mm, "radius": 6 * mm});
            skArc(sketch, "E82", {"start": v(-15, 120) * mm, "mid": v(0, 135) * mm, "end": v(15, 120) * mm});
            skLineSegment(sketch, "E83", {"start": v(-15, 120) * mm, "end": v(-15, 108) * mm});
            skLineSegment(sketch, "E84", {"start": v(15, 120) * mm, "end": v(15, 108) * mm});
            skLineSegment(sketch, "E85", {"start": v(-15, 108) * mm, "end": v(-33, 90) * mm});
            skLineSegment(sketch, "E86.MirrorCS", {"start": v(15, 108) * mm, "end": v(33, 90) * mm});
            skLineSegment(sketch, "E87", {"start": v(-80, 0) * mm, "end": v(80, 0) * mm, "construction": true});
            skCircle(sketch, "E88.MirrorC", {"center": v(0, -120) * mm, "radius": 6 * mm});
            skLineSegment(sketch, "E89.MirrorCS", {"start": v(-15, -120) * mm, "end": v(-15, -108) * mm});
            skPoint(sketch, "E90.MirrorP", {"position": v(0, -90) * mm});
            skArc(sketch, "E91.MirrorCS", {"start": v(-15, -120) * mm, "mid": v(0, -135) * mm, "end": v(15, -120) * mm});
            skLineSegment(sketch, "E92.MirrorCS", {"start": v(15, -120) * mm, "end": v(15, -108) * mm});
            skLineSegment(sketch, "E93.MirrorCS", {"start": v(15, -108) * mm, "end": v(33, -90) * mm});
            skLineSegment(sketch, "E94.MirrorCS", {"start": v(-15, -108) * mm, "end": v(-33, -90) * mm});
            skSolve(sketch);
        }
        {
            var Q0;
            Q0=makeQuery(id+"F16.imprint","IMPRINT",FACE,{"disambiguationData":[TD([[makeQuery(id+"F16.imprint","IMPRINT",EDGE,{"derivedFrom":sQuery(id+"F16.wireOp",EDGE,"E81")}),-1.0]])]});
            var Q1;
            Q1=makeQuery(id+"F16.imprint","IMPRINT",FACE,{"disambiguationData":[TD([[makeQuery(id+"F16.imprint","IMPRINT",EDGE,{"derivedFrom":makeQuery(id+"F1.opExtrude","CAP_EDGE",EDGE,{"disambiguationData":[OSD([sQuery(id+"F0.wireOp",EDGE,"E1.left")])],"isStart":true})}),-1.0]])]});
            var Q2;
            Q2=makeQuery(id+"F16.imprint","IMPRINT",FACE,{"disambiguationData":[TD([[makeQuery(id+"F16.imprint","IMPRINT",EDGE,{"derivedFrom":sQuery(id+"F16.wireOp",EDGE,"E88.MirrorC")}),1.0]])]});
            var Q3;
            Q3=makeQuery(id+"F2.opExtrude","CAP_FACE",FACE,{"disambiguationData":[OSD([sQuery(id+"F0.wireOp",EDGE,"E12"),sQuery(id+"F0.wireOp",EDGE,"E13"),sQuery(id+"F0.wireOp",EDGE,"E14"),sQuery(id+"F0.wireOp",EDGE,"E15"),sQuery(id+"F0.wireOp",EDGE,"E17.filletArc"),sQuery(id+"F0.wireOp",EDGE,"E18.filletArc"),sQuery(id+"F0.wireOp",EDGE,"E19.filletArc"),sQuery(id+"F0.wireOp",EDGE,"E20.filletArc"),sQuery(id+"F0.wireOp",EDGE,"E25.0"),sQuery(id+"F0.wireOp",EDGE,"E25.1"),sQuery(id+"F0.wireOp",EDGE,"E25.2"),sQuery(id+"F0.wireOp",EDGE,"E25.3"),sQuery(id+"F0.wireOp",EDGE,"E25.4"),sQuery(id+"F0.wireOp",EDGE,"E25.5"),sQuery(id+"F0.wireOp",EDGE,"E25.6"),sQuery(id+"F0.wireOp",EDGE,"E25.7")])],"isStart":false});
            extrude(context, id + "F17", {"entities" : qUnion([Q0, Q1, Q2]), "operationType" : NewBodyOperationType.ADD, "endBound" : BoundingType.UP_TO_SURFACE, "endBoundEntityFace" : qUnion([Q3]), "depth" : 25 * mm});
        }
    });
